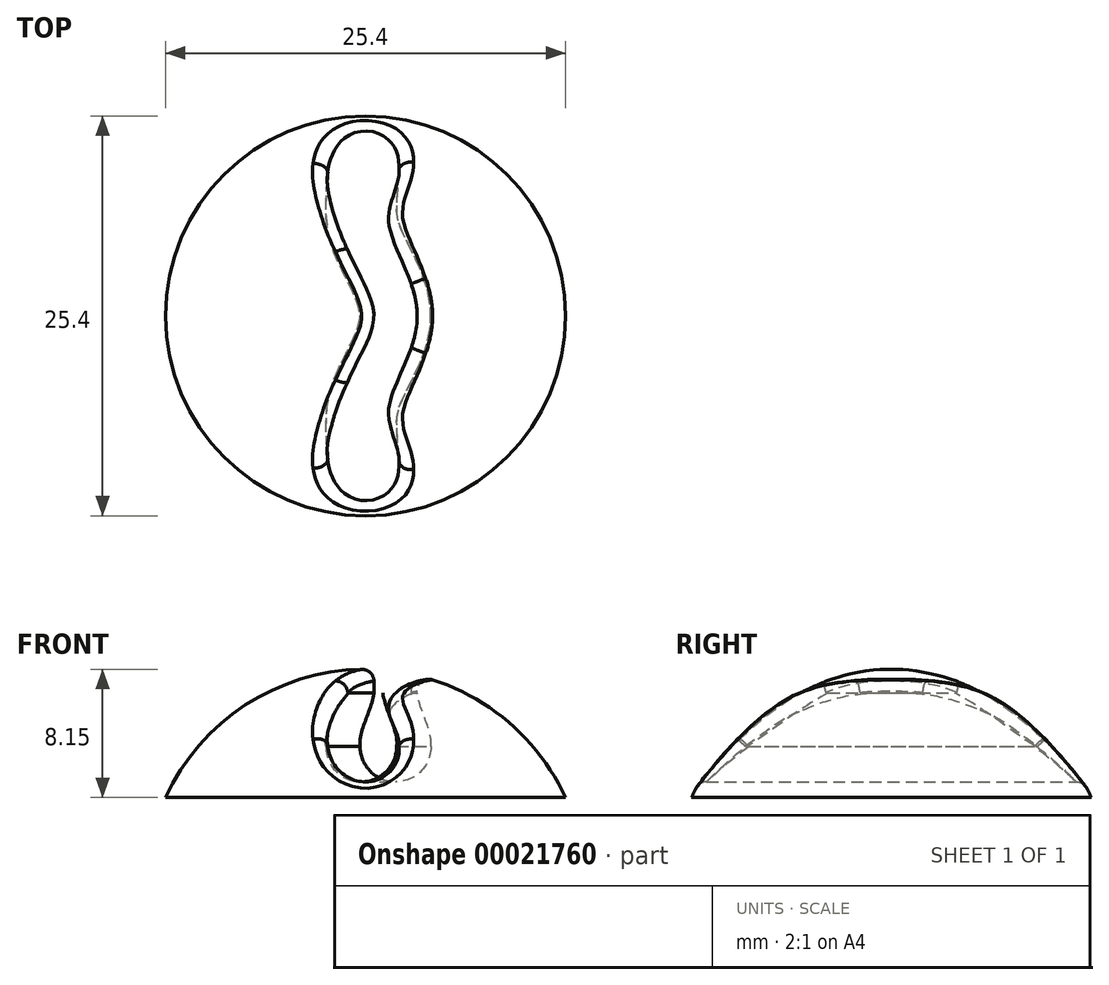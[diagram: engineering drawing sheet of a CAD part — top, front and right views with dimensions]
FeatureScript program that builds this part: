
annotation { "Feature Type Name" : "Feature", "Feature Type Description" : "" }
export const myFeature = defineFeature(function(context is Context, id is Id, definition is map)
    precondition{}
    {
        {
            var Q0;
            Q0=qCreatedBy(makeId("Front.planeOp"),FACE);
            var sketch = newSketch(context, id + "F0", { "sketchPlane" : qUnion([Q0])});
            skLineSegment(sketch, "E0", {"start": v(0, 0) * mm, "end": v(12.7, 0) * mm});
            skArc(sketch, "E1", {"start": v(12.7, 0) * mm, "mid": v(7.55, 5.94) * mm, "end": v(0, 8.15) * mm});
            skLineSegment(sketch, "E2", {"start": v(0, 8.15) * mm, "end": v(0, 0) * mm});
            skSolve(sketch);
        }
        {
            var Q0;
            Q0 = qSketchRegion(id + "F0", true);
            var Q1;
            Q1=sQuery(id+"F0.wireOp",EDGE,"E2");
            revolve(context, id + "F1", {"entities" : qUnion([Q0]), "axis" : qUnion([Q1]), "revolveType" : RevolveType.FULL});
        }
        {
            var Q0;
            Q0=qCreatedBy(makeId("Top.planeOp"),FACE);
            var sketch = newSketch(context, id + "F2", { "sketchPlane" : qUnion([Q0])});
            skCircle(sketch, "E3.0", {"center": v(0, 0) * mm, "radius": 12.7 * mm, "construction": true});
            skFitSpline(sketch, "E4", {"points": [v(0, -12.7) * mm, v(0, -5.08) * mm, v(1.9, 0) * mm, v(0, 5.08) * mm, v(0, 12.7) * mm], "startDerivative": vector(0, 49.17) * mm, "endDerivative": vector(0, 49.17) * mm});
            skSolve(sketch);
        }
        {
            var Q0;
            Q0=qCreatedBy(makeId("Front.planeOp"),FACE);
            cPlane(context, id + "F3", {"entities" : qUnion([Q0]), "cplaneType" : CPlaneType.OFFSET, "offset" : 12.7 * mm, "width" : 152.4 * mm, "height" : 152.4 * mm});
        }
        {
            var Q0;
            Q0=qCreatedBy(id+"F3.planeOp",FACE);
            var sketch = newSketch(context, id + "F4", { "sketchPlane" : qUnion([Q0])});
            skLineSegment(sketch, "E5", {"start": v(0, 8.15) * mm, "end": v(0, 0) * mm, "construction": true});
            skCircle(sketch, "E6", {"center": v(0, 3.25) * mm, "radius": 2.25 * mm});
            skFitSpline(sketch, "E7", {"points": [v(-2.25, 3.25) * mm, v(-1.38, 6.64) * mm, v(-1.94, 8.01) * mm], "startDerivative": vector(-0.69, 4.66) * mm, "endDerivative": vector(-3.55, -0.44) * mm});
            skFitSpline(sketch, "E8.MirrorCS", {"points": [v(2.25, 3.25) * mm, v(1.38, 6.64) * mm, v(1.94, 8.01) * mm], "startDerivative": vector(0.69, 4.66) * mm, "endDerivative": vector(3.55, -0.44) * mm});
            skLineSegment(sketch, "E9", {"start": v(-1.38, 6.64) * mm, "end": v(-1.38, 8.99) * mm});
            skLineSegment(sketch, "E10", {"start": v(-1.38, 8.99) * mm, "end": v(1.38, 8.99) * mm});
            skLineSegment(sketch, "E11", {"start": v(1.37, 8.99) * mm, "end": v(1.37, 6.64) * mm});
            skSolve(sketch);
        }
        {
            var Q0;
            Q0 = qSketchRegion(id + "F4", true);
            var Q1;
            Q1 = qConstructionFilter(qBodyType(qCreatedBy(id + "F2" ,EDGE), BodyType.WIRE), ConstructionObject.NO);
            sweep(context, id + "F5", {"operationType" : NewBodyOperationType.REMOVE, "profiles" : qUnion([Q0]), "path" : qUnion([Q1])});
        }
        {
            var Q0;
            Q0=makeQuery(id+"F5.boolean.opBoolean","INTERSECT",EDGE,{"disambiguationData":[OD(1.0)],"derivedFrom":[makeQuery(id+"F1.opRevolve","SWEPT_FACE",FACE,{"disambiguationData":[OSD([sQuery(id+"F0.wireOp",EDGE,"E1")])]}),makeQuery(id+"F5.opSweep","SWEPT_FACE",FACE,{"disambiguationData":[OSD([sQuery(id+"F2.wireOp",EDGE,"E4"),sQuery(id+"F4.wireOp",EDGE,"E7")])]})]});
            var Q1;
            Q1=makeQuery(id+"F5.boolean.opBoolean","INTERSECT",EDGE,{"derivedFrom":[makeQuery(id+"F1.opRevolve","SWEPT_FACE",FACE,{"disambiguationData":[OSD([sQuery(id+"F0.wireOp",EDGE,"E1")])]}),makeQuery(id+"F5.opSweep","SWEPT_FACE",FACE,{"disambiguationData":[OSD([sQuery(id+"F2.wireOp",EDGE,"E4"),sQuery(id+"F4.wireOp",EDGE,"E9")])]})]});
            var Q2;
            Q2=makeQuery(id+"F5.boolean.opBoolean","INTERSECT",EDGE,{"disambiguationData":[OD(0.0)],"derivedFrom":[makeQuery(id+"F1.opRevolve","SWEPT_FACE",FACE,{"disambiguationData":[OSD([sQuery(id+"F0.wireOp",EDGE,"E1")])]}),makeQuery(id+"F5.opSweep","SWEPT_FACE",FACE,{"disambiguationData":[OSD([sQuery(id+"F2.wireOp",EDGE,"E4"),sQuery(id+"F4.wireOp",EDGE,"E7")])]})]});
            var Q3;
            Q3=makeQuery(id+"F5.boolean.opBoolean","INTERSECT",EDGE,{"disambiguationData":[OD(0.0)],"derivedFrom":[makeQuery(id+"F1.opRevolve","SWEPT_FACE",FACE,{"disambiguationData":[OSD([sQuery(id+"F0.wireOp",EDGE,"E1")])]}),makeQuery(id+"F5.opSweep","SWEPT_FACE",FACE,{"disambiguationData":[OSD([sQuery(id+"F2.wireOp",EDGE,"E4"),sQuery(id+"F4.wireOp",EDGE,"E6")])]})]});
            var Q4;
            Q4=makeQuery(id+"F5.boolean.opBoolean","INTERSECT",EDGE,{"disambiguationData":[OD(0.0)],"derivedFrom":[makeQuery(id+"F1.opRevolve","SWEPT_FACE",FACE,{"disambiguationData":[OSD([sQuery(id+"F0.wireOp",EDGE,"E1")])]}),makeQuery(id+"F5.opSweep","SWEPT_FACE",FACE,{"disambiguationData":[OSD([sQuery(id+"F2.wireOp",EDGE,"E4"),sQuery(id+"F4.wireOp",EDGE,"E8.MirrorCS")])]})]});
            var Q5;
            Q5=makeQuery(id+"F5.boolean.opBoolean","INTERSECT",EDGE,{"derivedFrom":[makeQuery(id+"F1.opRevolve","SWEPT_FACE",FACE,{"disambiguationData":[OSD([sQuery(id+"F0.wireOp",EDGE,"E1")])]}),makeQuery(id+"F5.opSweep","SWEPT_FACE",FACE,{"disambiguationData":[OSD([sQuery(id+"F2.wireOp",EDGE,"E4"),sQuery(id+"F4.wireOp",EDGE,"E11")])]})]});
            var Q6;
            Q6=makeQuery(id+"F5.boolean.opBoolean","INTERSECT",EDGE,{"disambiguationData":[OD(1.0)],"derivedFrom":[makeQuery(id+"F1.opRevolve","SWEPT_FACE",FACE,{"disambiguationData":[OSD([sQuery(id+"F0.wireOp",EDGE,"E1")])]}),makeQuery(id+"F5.opSweep","SWEPT_FACE",FACE,{"disambiguationData":[OSD([sQuery(id+"F2.wireOp",EDGE,"E4"),sQuery(id+"F4.wireOp",EDGE,"E8.MirrorCS")])]})]});
            var Q7;
            Q7=makeQuery(id+"F5.boolean.opBoolean","INTERSECT",EDGE,{"disambiguationData":[OD(1.0)],"derivedFrom":[makeQuery(id+"F1.opRevolve","SWEPT_FACE",FACE,{"disambiguationData":[OSD([sQuery(id+"F0.wireOp",EDGE,"E1")])]}),makeQuery(id+"F5.opSweep","SWEPT_FACE",FACE,{"disambiguationData":[OSD([sQuery(id+"F2.wireOp",EDGE,"E4"),sQuery(id+"F4.wireOp",EDGE,"E6")])]})]});
            fillet(context, id + "F6", {"entities" : qUnion([Q0, Q1, Q2, Q3, Q4, Q5, Q6, Q7]), "radius" : 0.75 * mm, "tangentPropagation" : true, "allowEdgeOverflow" : false});
        }
    });
